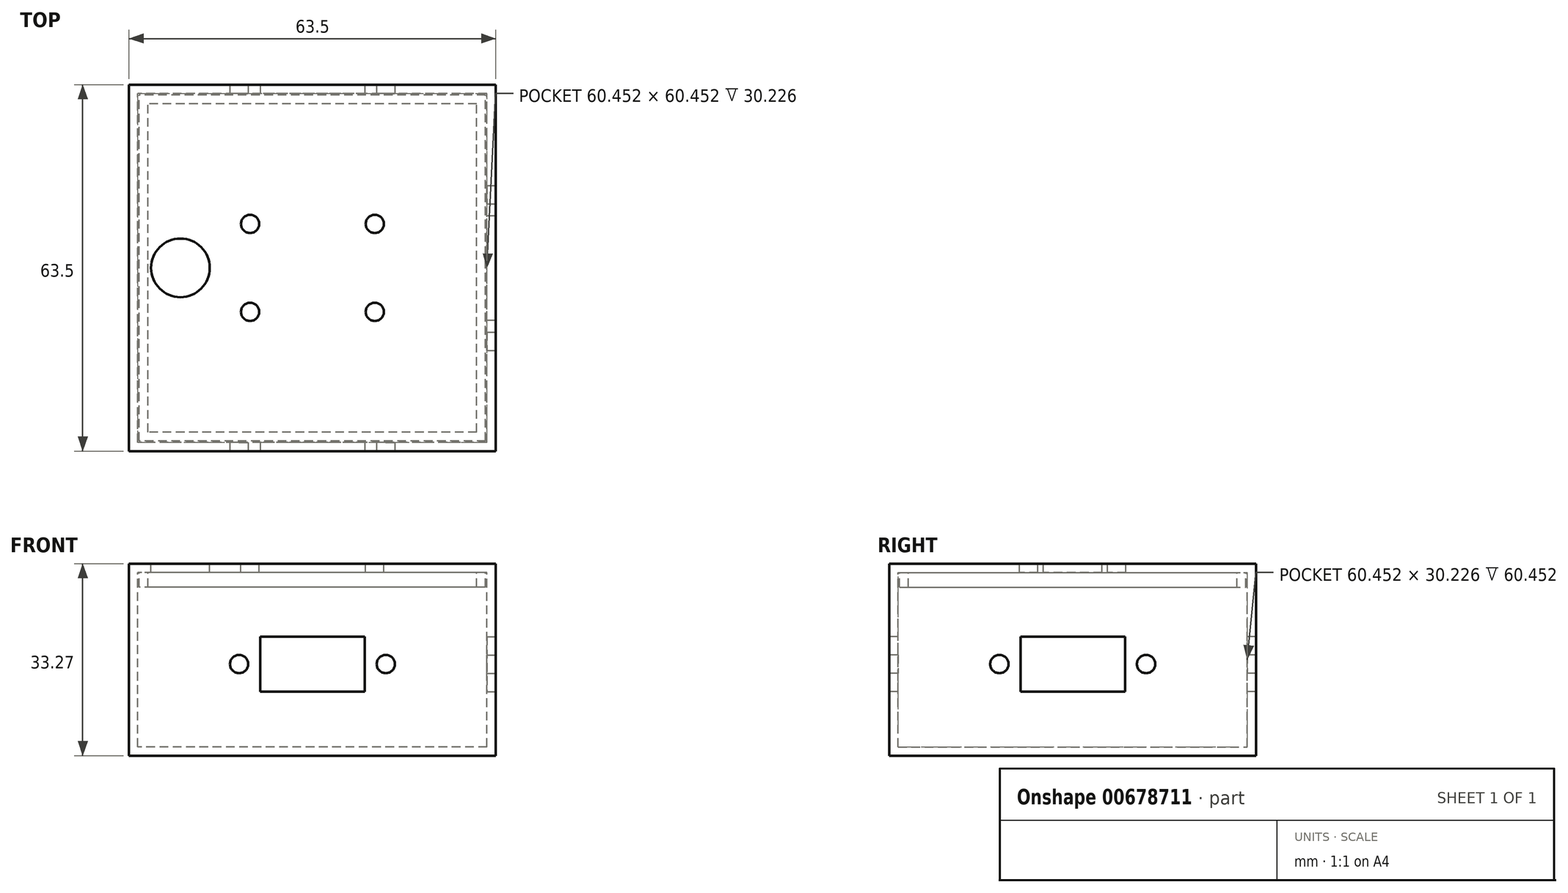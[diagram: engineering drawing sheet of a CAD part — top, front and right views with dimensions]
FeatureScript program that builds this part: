
annotation { "Feature Type Name" : "Feature", "Feature Type Description" : "" }
export const myFeature = defineFeature(function(context is Context, id is Id, definition is map)
    precondition{}
    {
        {
            var Q0;
            Q0=qCreatedBy(makeId("Top.planeOp"),FACE);
            var sketch = newSketch(context, id + "F0", { "sketchPlane" : qUnion([Q0])});
            skLineSegment(sketch, "E0.bottom", {"start": v(31.75, -31.75) * mm, "end": v(-31.75, -31.75) * mm});
            skLineSegment(sketch, "E0.top", {"start": v(31.75, 31.75) * mm, "end": v(-31.75, 31.75) * mm});
            skLineSegment(sketch, "E0.left", {"start": v(31.75, -31.75) * mm, "end": v(31.75, 31.75) * mm});
            skLineSegment(sketch, "E0.right", {"start": v(-31.75, -31.75) * mm, "end": v(-31.75, 31.75) * mm});
            skPoint(sketch, "E0.middle", {"position": v(0, 0) * mm});
            skSolve(sketch);
        }
        {
            var Q0;
            Q0 = qSketchRegion(id + "F0", true);
            extrude(context, id + "F1", {"entities" : qUnion([Q0]), "depth" : 31.75 * mm, "offsetDistance" : 25.4 * mm});
        }
        {
            var Q0;
            Q0=makeQuery(id+"F1.opExtrude","CAP_FACE",FACE,{"disambiguationData":[OSD([sQuery(id+"F0.wireOp",EDGE,"E0.bottom"),sQuery(id+"F0.wireOp",EDGE,"E0.top"),sQuery(id+"F0.wireOp",EDGE,"E0.left"),sQuery(id+"F0.wireOp",EDGE,"E0.right")])],"isStart":false});
            var sketch = newSketch(context, id + "F2", { "sketchPlane" : qUnion([Q0])});
            skLineSegment(sketch, "E1.0", {"start": v(30.23, -30.23) * mm, "end": v(-30.23, -30.23) * mm});
            skLineSegment(sketch, "E1.1", {"start": v(30.23, -30.23) * mm, "end": v(30.23, 30.23) * mm});
            skLineSegment(sketch, "E1.2", {"start": v(30.23, 30.23) * mm, "end": v(-30.23, 30.23) * mm});
            skLineSegment(sketch, "E1.3", {"start": v(-30.23, -30.23) * mm, "end": v(-30.23, 30.23) * mm});
            skSolve(sketch);
        }
        {
            var Q0;
            Q0=makeQuery(id+"F2.imprint","IMPRINT",FACE,{"disambiguationData":[TD([[makeQuery(id+"F2.imprint","IMPRINT",EDGE,{"derivedFrom":sQuery(id+"F2.wireOp",EDGE,"E1.0")}),-1.0]])]});
            extrude(context, id + "F3", {"entities" : qUnion([Q0]), "operationType" : NewBodyOperationType.REMOVE, "oppositeDirection" : true, "depth" : 30.23 * mm, "offsetDistance" : 25.4 * mm});
        }
        {
            var Q0;
            Q0=makeQuery(id+"F1.opExtrude","SWEPT_FACE",FACE,{"disambiguationData":[OSD([sQuery(id+"F0.wireOp",EDGE,"E0.bottom")])]});
            var sketch = newSketch(context, id + "F4", { "sketchPlane" : qUnion([Q0])});
            skLineSegment(sketch, "E2", {"start": v(0, 0) * mm, "end": v(0, 31.75) * mm});
            skLineSegment(sketch, "E3.bottom", {"start": v(-9.05, 20.64) * mm, "end": v(9.05, 20.64) * mm});
            skLineSegment(sketch, "E3.top", {"start": v(-9.05, 11.11) * mm, "end": v(9.05, 11.11) * mm});
            skLineSegment(sketch, "E3.left", {"start": v(-9.05, 20.64) * mm, "end": v(-9.05, 11.11) * mm});
            skLineSegment(sketch, "E3.right", {"start": v(9.05, 20.64) * mm, "end": v(9.05, 11.11) * mm});
            skPoint(sketch, "E3.middle", {"position": v(0, 15.88) * mm});
            skCircle(sketch, "E4", {"center": v(-12.7, 15.88) * mm, "radius": 1.59 * mm});
            skCircle(sketch, "E5.MirrorC", {"center": v(12.7, 15.88) * mm, "radius": 1.59 * mm});
            skSolve(sketch);
        }
        {
            var Q0;
            Q0 = qSketchRegion(id + "F4", true);
            extrude(context, id + "F5", {"entities" : qUnion([Q0]), "operationType" : NewBodyOperationType.REMOVE, "oppositeDirection" : true, "depth" : 76.2 * mm, "offsetDistance" : 25.4 * mm});
        }
        {
            var Q0;
            Q0=makeQuery(id+"F1.opExtrude","SWEPT_FACE",FACE,{"disambiguationData":[OSD([sQuery(id+"F0.wireOp",EDGE,"E0.left")])]});
            var sketch = newSketch(context, id + "F6", { "sketchPlane" : qUnion([Q0])});
            skLineSegment(sketch, "E6", {"start": v(0, 0) * mm, "end": v(0, 31.75) * mm});
            skLineSegment(sketch, "E7.bottom", {"start": v(-9.05, 20.64) * mm, "end": v(9.05, 20.64) * mm});
            skLineSegment(sketch, "E7.top", {"start": v(-9.05, 11.11) * mm, "end": v(9.05, 11.11) * mm});
            skLineSegment(sketch, "E7.left", {"start": v(-9.05, 20.64) * mm, "end": v(-9.05, 11.11) * mm});
            skLineSegment(sketch, "E7.right", {"start": v(9.05, 20.64) * mm, "end": v(9.05, 11.11) * mm});
            skPoint(sketch, "E7.middle", {"position": v(0, 15.88) * mm});
            skCircle(sketch, "E8", {"center": v(-12.7, 15.88) * mm, "radius": 1.59 * mm});
            skCircle(sketch, "E9.MirrorC", {"center": v(12.7, 15.88) * mm, "radius": 1.59 * mm});
            skSolve(sketch);
        }
        {
            var Q0;
            Q0 = qSketchRegion(id + "F6", true);
            extrude(context, id + "F7", {"entities" : qUnion([Q0]), "operationType" : NewBodyOperationType.REMOVE, "oppositeDirection" : true, "depth" : 25.4 * mm, "offsetDistance" : 25.4 * mm});
        }
        {
            var Q0;
            Q0=makeQuery(id+"F1.opExtrude","CAP_FACE",FACE,{"disambiguationData":[OSD([sQuery(id+"F0.wireOp",EDGE,"E0.bottom"),sQuery(id+"F0.wireOp",EDGE,"E0.top"),sQuery(id+"F0.wireOp",EDGE,"E0.left"),sQuery(id+"F0.wireOp",EDGE,"E0.right")])],"isStart":false});
            var sketch = newSketch(context, id + "F8", { "sketchPlane" : qUnion([Q0])});
            skLineSegment(sketch, "E10.0", {"start": v(29.97, -29.97) * mm, "end": v(-29.97, -29.97) * mm});
            skLineSegment(sketch, "E10.1", {"start": v(29.97, -29.97) * mm, "end": v(29.97, 29.97) * mm});
            skLineSegment(sketch, "E10.2", {"start": v(29.97, 29.97) * mm, "end": v(-29.97, 29.97) * mm});
            skLineSegment(sketch, "E10.3", {"start": v(-29.97, -29.97) * mm, "end": v(-29.97, 29.97) * mm});
            skLineSegment(sketch, "E11.0", {"start": v(28.45, -28.45) * mm, "end": v(-28.45, -28.45) * mm});
            skLineSegment(sketch, "E11.1", {"start": v(28.45, -28.45) * mm, "end": v(28.45, 28.45) * mm});
            skLineSegment(sketch, "E11.2", {"start": v(28.45, 28.45) * mm, "end": v(-28.45, 28.45) * mm});
            skLineSegment(sketch, "E11.3", {"start": v(-28.45, -28.45) * mm, "end": v(-28.45, 28.45) * mm});
            skSolve(sketch);
        }
        {
            var Q0;
            Q0 = qSketchRegion(id + "F8", true);
            extrude(context, id + "F9", {"entities" : qUnion([Q0]), "oppositeDirection" : true, "depth" : 2.54 * mm, "offsetDistance" : 25.4 * mm});
        }
        {
            var Q0;
            Q0=makeQuery(id+"F1.opExtrude","CAP_FACE",FACE,{"disambiguationData":[OSD([sQuery(id+"F0.wireOp",EDGE,"E0.bottom"),sQuery(id+"F0.wireOp",EDGE,"E0.top"),sQuery(id+"F0.wireOp",EDGE,"E0.left"),sQuery(id+"F0.wireOp",EDGE,"E0.right")])],"isStart":false});
            var sketch = newSketch(context, id + "F10", { "sketchPlane" : qUnion([Q0])});
            skLineSegment(sketch, "E12.bottom", {"start": v(-31.75, -31.75) * mm, "end": v(31.75, -31.75) * mm});
            skLineSegment(sketch, "E12.top", {"start": v(-31.75, 31.75) * mm, "end": v(31.75, 31.75) * mm});
            skLineSegment(sketch, "E12.left", {"start": v(-31.75, -31.75) * mm, "end": v(-31.75, 31.75) * mm});
            skLineSegment(sketch, "E12.right", {"start": v(31.75, -31.75) * mm, "end": v(31.75, 31.75) * mm});
            skSolve(sketch);
        }
        {
            var Q0;
            Q0 = qSketchRegion(id + "F10", true);
            extrude(context, id + "F11", {"entities" : qUnion([Q0]), "operationType" : NewBodyOperationType.ADD, "depth" : 1.52 * mm, "offsetDistance" : 25.4 * mm});
        }
        {
            var Q0;
            Q0=makeQuery(id+"F11.opExtrude","CAP_FACE",FACE,{"disambiguationData":[OSD([sQuery(id+"F10.wireOp",EDGE,"E12.bottom"),sQuery(id+"F10.wireOp",EDGE,"E12.top"),sQuery(id+"F10.wireOp",EDGE,"E12.left"),sQuery(id+"F10.wireOp",EDGE,"E12.right")])],"isStart":false});
            var sketch = newSketch(context, id + "F12", { "sketchPlane" : qUnion([Q0])});
            skLineSegment(sketch, "E13.bottom", {"start": v(10.8, 7.62) * mm, "end": v(-10.8, 7.62) * mm});
            skLineSegment(sketch, "E13.top", {"start": v(10.8, -7.62) * mm, "end": v(-10.8, -7.62) * mm});
            skLineSegment(sketch, "E13.left", {"start": v(10.8, 7.62) * mm, "end": v(10.8, -7.62) * mm});
            skLineSegment(sketch, "E13.right", {"start": v(-10.8, 7.62) * mm, "end": v(-10.8, -7.62) * mm});
            skPoint(sketch, "E13.middle", {"position": v(0, 0) * mm});
            skCircle(sketch, "E14", {"center": v(-10.8, -7.62) * mm, "radius": 1.59 * mm});
            skCircle(sketch, "E15", {"center": v(-10.8, 7.62) * mm, "radius": 1.59 * mm});
            skCircle(sketch, "E16", {"center": v(10.8, 7.62) * mm, "radius": 1.59 * mm});
            skCircle(sketch, "E17", {"center": v(10.8, -7.62) * mm, "radius": 1.59 * mm});
            skCircle(sketch, "E18", {"center": v(-22.86, 0) * mm, "radius": 5.08 * mm});
            skSolve(sketch);
        }
        {
            var Q0;
            {var subQ0=sQuery(id+"F12.wireOp",EDGE,"E13.left");var subQ1=sQuery(id+"F12.wireOp",EDGE,"E13.bottom");var subQ2=makeQuery(id+"F12.imprint","INTERSECT",VERTEX,{"derivedFrom":[subQ1,subQ0]});Q0=makeQuery(id+"F12.imprint","IMPRINT",FACE,{"disambiguationData":[TD([[makeQuery(id+"F12.imprint","IMPRINT",EDGE,{"disambiguationData":[TD([[subQ2,-1.0]])],"derivedFrom":subQ1}),1.0]])]});}
            var Q1;
            {var subQ0=sQuery(id+"F12.wireOp",EDGE,"E13.left");var subQ1=sQuery(id+"F12.wireOp",EDGE,"E13.bottom");var subQ2=makeQuery(id+"F12.imprint","INTERSECT",VERTEX,{"derivedFrom":[subQ1,subQ0]});Q1=makeQuery(id+"F12.imprint","IMPRINT",FACE,{"disambiguationData":[TD([[makeQuery(id+"F12.imprint","IMPRINT",EDGE,{"disambiguationData":[TD([[subQ2,-1.0]])],"derivedFrom":subQ1}),-1.0]])]});}
            var Q2;
            {var subQ0=sQuery(id+"F12.wireOp",EDGE,"E13.right");var subQ1=sQuery(id+"F12.wireOp",EDGE,"E13.bottom");var subQ2=makeQuery(id+"F12.imprint","INTERSECT",VERTEX,{"derivedFrom":[subQ1,subQ0]});Q2=makeQuery(id+"F12.imprint","IMPRINT",FACE,{"disambiguationData":[TD([[makeQuery(id+"F12.imprint","IMPRINT",EDGE,{"disambiguationData":[TD([[subQ2,1.0]])],"derivedFrom":subQ1}),-1.0]])]});}
            var Q3;
            {var subQ0=sQuery(id+"F12.wireOp",EDGE,"E13.right");var subQ1=sQuery(id+"F12.wireOp",EDGE,"E13.bottom");var subQ2=makeQuery(id+"F12.imprint","INTERSECT",VERTEX,{"derivedFrom":[subQ1,subQ0]});Q3=makeQuery(id+"F12.imprint","IMPRINT",FACE,{"disambiguationData":[TD([[makeQuery(id+"F12.imprint","IMPRINT",EDGE,{"disambiguationData":[TD([[subQ2,1.0]])],"derivedFrom":subQ1}),1.0]])]});}
            var Q4;
            {var subQ0=sQuery(id+"F12.wireOp",EDGE,"E13.left");var subQ1=sQuery(id+"F12.wireOp",EDGE,"E13.top");var subQ2=makeQuery(id+"F12.imprint","INTERSECT",VERTEX,{"derivedFrom":[subQ1,subQ0]});Q4=makeQuery(id+"F12.imprint","IMPRINT",FACE,{"disambiguationData":[TD([[makeQuery(id+"F12.imprint","IMPRINT",EDGE,{"disambiguationData":[TD([[subQ2,-1.0]])],"derivedFrom":subQ1}),-1.0]])]});}
            var Q5;
            {var subQ0=sQuery(id+"F12.wireOp",EDGE,"E13.left");var subQ1=sQuery(id+"F12.wireOp",EDGE,"E13.top");var subQ2=makeQuery(id+"F12.imprint","INTERSECT",VERTEX,{"derivedFrom":[subQ1,subQ0]});Q5=makeQuery(id+"F12.imprint","IMPRINT",FACE,{"disambiguationData":[TD([[makeQuery(id+"F12.imprint","IMPRINT",EDGE,{"disambiguationData":[TD([[subQ2,-1.0]])],"derivedFrom":subQ1}),1.0]])]});}
            var Q6;
            {var subQ0=sQuery(id+"F12.wireOp",EDGE,"E13.right");var subQ1=sQuery(id+"F12.wireOp",EDGE,"E13.top");var subQ2=makeQuery(id+"F12.imprint","INTERSECT",VERTEX,{"derivedFrom":[subQ1,subQ0]});Q6=makeQuery(id+"F12.imprint","IMPRINT",FACE,{"disambiguationData":[TD([[makeQuery(id+"F12.imprint","IMPRINT",EDGE,{"disambiguationData":[TD([[subQ2,1.0]])],"derivedFrom":subQ1}),-1.0]])]});}
            var Q7;
            {var subQ0=sQuery(id+"F12.wireOp",EDGE,"E13.right");var subQ1=sQuery(id+"F12.wireOp",EDGE,"E13.top");var subQ2=makeQuery(id+"F12.imprint","INTERSECT",VERTEX,{"derivedFrom":[subQ1,subQ0]});Q7=makeQuery(id+"F12.imprint","IMPRINT",FACE,{"disambiguationData":[TD([[makeQuery(id+"F12.imprint","IMPRINT",EDGE,{"disambiguationData":[TD([[subQ2,1.0]])],"derivedFrom":subQ1}),1.0]])]});}
            var Q8;
            Q8=makeQuery(id+"F12.imprint","IMPRINT",FACE,{"disambiguationData":[TD([[makeQuery(id+"F12.imprint","IMPRINT",EDGE,{"derivedFrom":sQuery(id+"F12.wireOp",EDGE,"E18")}),1.0]])]});
            extrude(context, id + "F13", {"entities" : qUnion([Q0, Q1, Q2, Q3, Q4, Q5, Q6, Q7, Q8]), "operationType" : NewBodyOperationType.REMOVE, "oppositeDirection" : true, "depth" : 25.4 * mm, "offsetDistance" : 25.4 * mm});
        }
    });
